FCSTD DOCUMENT  (FreeCAD 0.20R29410 (Git))
Label: plan
License: All rights reserved
LicenseURL: http://en.wikipedia.org/wiki/All_rights_reserved
objects: Sketcher::SketchObject×1, PartDesign::Body×1, Spreadsheet::Sheet×1
note: 2 computed .brp shape members not serialized (recipe doc carries the construction recipe); baked Part::Feature solids carry a one-line shape summary decoded from their .brp

FEATURE [Sketcher::SketchObject] Sketch
  FullyConstrained = true
  MapMode = 5
  Placement = pos=(0,0,0) rot=(1,0,0;1.5708rad)
  Support = -> [XZ_Plane]
  expr: Constraints[105] = <<plan>>#<<data>>.plug_height_adat
  expr: Constraints[114] = <<plan>>#<<data>>.output_h
  expr: Constraints[115] = <<plan>>#<<data>>.output_d
  expr: Constraints[116] = <<plan>>#<<data>>.base_t
  expr: Constraints[157] = <<plan>>#<<data>>.wall_t * 2
  expr: Constraints[173] = <<plan>>#<<data>>.top_row_d
  expr: Constraints[175] = <<plan>>#<<data>>.bot_row_d
  expr: Constraints[176] = <<plan>>#<<data>>.middle_space_d
  expr: Constraints[177] = <<plan>>#<<data>>.topbot_latch_d
  expr: Constraints[183] = <<plan>>#<<data>>.wall_t
  expr: Constraints[189] = <<plan>>#<<data>>.plug_height_audio + <<plan>>#<<data>>.wall_t
  expr: Constraints[190] = <<plan>>#<<data>>.plug_height_usb + <<plan>>#<<data>>.wall_t
  expr: Constraints[6] = <<plan>>#<<data>>.central_d
  expr: Constraints[78] = <<plan>>#<<data>>.plug_height_audio
  expr: Constraints[79] = <<plan>>#<<data>>.es3_h
  expr: Constraints[7] = <<plan>>#<<data>>.central_h
  expr: Constraints[80] = <<plan>>#<<data>>.es6_h
  expr: Constraints[81] = <<plan>>#<<data>>.es7_h
  expr: Constraints[82] = <<plan>>#<<data>>.es3_d
  expr: Constraints[83] = <<plan>>#<<data>>.es6_d
  expr: Constraints[84] = <<plan>>#<<data>>.es7_d
  expr: Constraints[85] = <<plan>>#<<data>>.wall_t
  expr: Constraints[86] = <<plan>>#<<data>>.base_t
  expr: Constraints[87] = <<plan>>#<<data>>.base_t
  expr: Constraints[8] = <<plan>>#<<data>>.case_d
  expr: Constraints[94] = <<plan>>#<<data>>.mungo_d
  expr: Constraints[95] = <<plan>>#<<data>>.mungo_h
  expr: Constraints[96] = <<plan>>#<<data>>.rme_d
  expr: Constraints[97] = <<plan>>#<<data>>.rme_h
  sketch-geometry (67):
    g0: LineSegment StartX=-3.67e-14 StartY=123.2 StartZ=0 EndX=277 EndY=123.2 EndZ=0
    g1: LineSegment StartX=273 StartY=58.2 StartZ=0 EndX=273 EndY=53.2 EndZ=0
    g2: LineSegment StartX=4 StartY=53.2 StartZ=0 EndX=4 EndY=58.2 EndZ=0
    g3: LineSegment StartX=24 StartY=32.88 StartZ=0 EndX=79 EndY=32.88 EndZ=0
    g4: LineSegment StartX=79 StartY=32.88 StartZ=0 EndX=79 EndY=10.88 EndZ=0
    g5: LineSegment StartX=79 StartY=10.88 StartZ=0 EndX=24 EndY=10.88 EndZ=0
    g6: LineSegment StartX=24 StartY=10.88 StartZ=0 EndX=24 EndY=32.88 EndZ=0
    g7: LineSegment StartX=139 StartY=78.2 StartZ=0 EndX=214 EndY=78.2 EndZ=0
    g8: LineSegment StartX=214 StartY=78.2 StartZ=0 EndX=214 EndY=58.2 EndZ=0
    g9: LineSegment StartX=214 StartY=58.2 StartZ=0 EndX=139 EndY=58.2 EndZ=0
    g10: LineSegment StartX=139 StartY=58.2 StartZ=0 EndX=139 EndY=78.2 EndZ=0
    g11: LineSegment StartX=8 StartY=57.88 StartZ=0 EndX=83 EndY=57.88 EndZ=0
    g12: LineSegment StartX=83 StartY=57.88 StartZ=0 EndX=83 EndY=37.88 EndZ=0
    g13: LineSegment StartX=83 StartY=37.88 StartZ=0 EndX=8 EndY=37.88 EndZ=0
    g14: LineSegment StartX=8 StartY=37.88 StartZ=0 EndX=8 EndY=57.88 EndZ=0
    g15: LineSegment StartX=139 StartY=43.04 StartZ=0 EndX=196 EndY=43.04 EndZ=0
    g16: LineSegment StartX=196 StartY=43.04 StartZ=0 EndX=196 EndY=2.4 EndZ=0
    g17: LineSegment StartX=196 StartY=2.4 StartZ=0 EndX=139 EndY=2.4 EndZ=0
    g18: LineSegment StartX=139 StartY=2.4 StartZ=0 EndX=139 EndY=43.04 EndZ=0
    g19: LineSegment StartX=196 StartY=53.2 StartZ=0 EndX=253 EndY=53.2 EndZ=0
    g20: LineSegment StartX=253 StartY=53.2 StartZ=0 EndX=253 EndY=22.72 EndZ=0
    g21: LineSegment StartX=253 StartY=22.72 StartZ=0 EndX=196 EndY=22.72 EndZ=0
    g22: LineSegment StartX=196 StartY=22.72 StartZ=0 EndX=196 EndY=53.2 EndZ=0
    g23: LineSegment StartX=139 StartY=2.4 StartZ=0 EndX=119 EndY=2.4 EndZ=0
    g24: LineSegment StartX=119 StartY=2.4 StartZ=0 EndX=119 EndY=43.04 EndZ=0
    g25: LineSegment StartX=119 StartY=43.04 StartZ=0 EndX=139 EndY=43.04 EndZ=0
    g26: LineSegment StartX=253 StartY=53.2 StartZ=0 EndX=273 EndY=53.2 EndZ=0
    g27: LineSegment StartX=273 StartY=53.2 StartZ=0 EndX=273 EndY=22.72 EndZ=0
    g28: LineSegment StartX=273 StartY=22.72 StartZ=0 EndX=253 EndY=22.72 EndZ=0
    g29: LineSegment StartX=196 StartY=22.72 StartZ=0 EndX=253 EndY=22.72 EndZ=0
    g30: LineSegment StartX=253 StartY=22.72 StartZ=0 EndX=253 EndY=2.4 EndZ=0
    g31: LineSegment StartX=253 StartY=2.4 StartZ=0 EndX=196 EndY=2.4 EndZ=0
    g32: LineSegment StartX=196 StartY=2.4 StartZ=0 EndX=196 EndY=22.72 EndZ=0
    g33: LineSegment StartX=253 StartY=2.4 StartZ=0 EndX=273 EndY=2.4 EndZ=0
    g34: LineSegment StartX=273 StartY=2.4 StartZ=0 EndX=273 EndY=22.72 EndZ=0
    g35: LineSegment StartX=273 StartY=22.72 StartZ=0 EndX=253 EndY=22.72 EndZ=0
    g36: LineSegment StartX=79 StartY=32.88 StartZ=0 EndX=119 EndY=32.88 EndZ=0
    g37: LineSegment StartX=119 StartY=32.88 StartZ=0 EndX=119 EndY=10.88 EndZ=0
    g38: LineSegment StartX=119 StartY=10.88 StartZ=0 EndX=79 EndY=10.88 EndZ=0
    g39: LineSegment StartX=24 StartY=32.88 StartZ=0 EndX=81 EndY=32.88 EndZ=0
    g40: LineSegment StartX=81 StartY=32.88 StartZ=0 EndX=81 EndY=2.4 EndZ=0
    g41: LineSegment StartX=81 StartY=2.4 StartZ=0 EndX=24 EndY=2.4 EndZ=0
    g42: LineSegment StartX=24 StartY=2.4 StartZ=0 EndX=24 EndY=32.88 EndZ=0
    g43: LineSegment StartX=24 StartY=32.88 StartZ=0 EndX=24 EndY=32.88 EndZ=0
    g44: LineSegment StartX=24 StartY=32.88 StartZ=0 EndX=24 EndY=10.88 EndZ=0
    g45: LineSegment StartX=24 StartY=10.88 StartZ=0 EndX=24 EndY=10.88 EndZ=0
    g46: LineSegment StartX=119 StartY=53.2 StartZ=0 EndX=119 EndY=2.4 EndZ=0
    g47: LineSegment StartX=119 StartY=2.4 StartZ=0 EndX=114 EndY=2.4 EndZ=0
    g48: LineSegment StartX=114 StartY=53.2 StartZ=0 EndX=114 EndY=58.2 EndZ=0
    g49: LineSegment StartX=273 StartY=53.2 StartZ=0 EndX=119 EndY=53.2 EndZ=0
    g50: LineSegment StartX=119 StartY=53.2 StartZ=0 EndX=4 EndY=53.2 EndZ=0
    g51: LineSegment StartX=4 StartY=58.2 StartZ=0 EndX=114 EndY=58.2 EndZ=0
    g52: LineSegment StartX=114 StartY=58.2 StartZ=0 EndX=273 EndY=58.2 EndZ=0
    g53: LineSegment StartX=114 StartY=32.88 StartZ=0 EndX=4 EndY=32.88 EndZ=0
    g54: LineSegment StartX=4 StartY=32.88 StartZ=0 EndX=4 EndY=37.88 EndZ=0
    g55: LineSegment StartX=4 StartY=37.88 StartZ=0 EndX=114 EndY=37.88 EndZ=0
    g56: LineSegment StartX=114 StartY=37.88 StartZ=0 EndX=114 EndY=53.2 EndZ=0
    g57: LineSegment StartX=114 StartY=2.4 StartZ=0 EndX=114 EndY=32.88 EndZ=0
    g58: LineSegment StartX=114 StartY=32.88 StartZ=0 EndX=114 EndY=37.88 EndZ=0
    g59: LineSegment StartX=8 StartY=123.2 StartZ=0 EndX=8 EndY=58.2 EndZ=0
    g60: LineSegment StartX=8 StartY=58.2 StartZ=0 EndX=136.5 EndY=58.2 EndZ=0
    g61: LineSegment StartX=136.5 StartY=58.2 StartZ=0 EndX=136.5 EndY=123.2 EndZ=0
    g62: LineSegment StartX=140.5 StartY=123.2 StartZ=0 EndX=140.5 EndY=78.2 EndZ=0
    g63: LineSegment StartX=140.5 StartY=78.2 StartZ=0 EndX=269 EndY=78.2 EndZ=0
    g64: LineSegment StartX=269 StartY=78.2 StartZ=0 EndX=269 EndY=123.2 EndZ=0
    g65: LineSegment StartX=0 StartY=0 StartZ=0 EndX=277 EndY=0 EndZ=0
    g66: LineSegment StartX=277 StartY=0 StartZ=0 EndX=277 EndY=123.2 EndZ=0
  constraints (191):
    c: Coincident(g52,g1)
    c: Coincident(g1,g49)
    c: Coincident(g50,g2)
    c: Coincident(g2,g51)
    c: Vertical(g1)
    c: Vertical(g2)
    c: DistanceX(g51,g52) = 269
    c: DistanceY(g2,g2) = 5
    c: Distance(g0) = 277
    c: Coincident(g3,g4)
    c: Coincident(g4,g5)
    c: Coincident(g5,g6)
    c: Coincident(g6,g3)
    c: Horizontal(g3)
    c: Horizontal(g5)
    c: Vertical(g4)
    c: Vertical(g6)
    c: Coincident(g7,g8)
    c: Coincident(g8,g9)
    c: Coincident(g9,g10)
    c: Coincident(g10,g7)
    c: Horizontal(g7)
    c: Horizontal(g9)
    c: Vertical(g8)
    c: Vertical(g10)
    c: Coincident(g11,g12)
    c: Coincident(g12,g13)
    c: Coincident(g13,g14)
    c: Coincident(g14,g11)
    c: Horizontal(g11)
    c: Horizontal(g13)
    c: Vertical(g12)
    c: Vertical(g14)
    c: Coincident(g15,g16)
    c: Coincident(g16,g17)
    c: Coincident(g17,g18)
    c: Coincident(g18,g15)
    c: Horizontal(g15)
    c: Horizontal(g17)
    c: Vertical(g16)
    c: Coincident(g19,g20)
    c: Coincident(g20,g21)
    c: Coincident(g21,g22)
    c: Coincident(g22,g19)
    c: Horizontal(g19)
    c: Horizontal(g21)
    c: Vertical(g20)
    c: Vertical(g22)
    c: Coincident(g17,g23)
    c: Horizontal(g23)
    c: Coincident(g23,g24)
    c: Vertical(g24)
    c: Coincident(g24,g25)
    c: Coincident(g25,g15)
    c: Horizontal(g25)
    c: Coincident(g19,g26)
    c: Horizontal(g26)
    c: Coincident(g26,g27)
    c: Vertical(g27)
    c: Coincident(g27,g28)
    c: Horizontal(g28)
    c: Coincident(g29,g30)
    c: Coincident(g30,g31)
    c: Coincident(g31,g32)
    c: Coincident(g32,g29)
    c: Horizontal(g29)
    c: Horizontal(g31)
    c: Vertical(g30)
    c: Vertical(g32)
    c: Coincident(g30,g33)
    c: Horizontal(g33)
    c: Coincident(g33,g34)
    c: Vertical(g34)
    c: Coincident(g34,g35)
    c: Coincident(g35,g29)
    c: Horizontal(g35)
    c: Equal(g25,g26)
    c: Equal(g26,g35)
    c: Distance(g25) = 20
    c: Distance(g18) = 40.64
    c: Distance(g20) = 30.48
    c: Distance(g30) = 20.32
    c: Distance(g15) = 57
    c: Distance(g19) = 57
    c: Distance(g29) = 57
    c: DistanceX(g-2,g50) = 4
    c: DistanceY(g17) = 2.4
    c: DistanceY(g-1,g30) = 2.4
    c: Coincident(g28,g20)
    c: Coincident(g29,g20)
    c: PointOnObject(g31,g16)
    c: PointOnObject(g26,g1)
    c: Equal(g7,g11)
    c: Equal(g8,g14)
    c: Distance(g11) = 75
    c: Distance(g14) = 20
    c: Distance(g3) = 55
    c: Distance(g6) = 22
    c: Coincident(g3,g36)
    c: Horizontal(g36)
    c: Coincident(g36,g37)
    c: Vertical(g37)
    c: Coincident(g37,g38)
    c: Coincident(g38,g4)
    c: Horizontal(g38)
    c: Distance(g36) = 40
    c: Coincident(g39,g40)
    c: Coincident(g40,g41)
    c: Coincident(g41,g42)
    c: Coincident(g42,g39)
    c: Horizontal(g39)
    c: Horizontal(g41)
    c: Vertical(g40)
    c: Vertical(g42)
    c: Distance(g42) = 30.48
    c: Distance(g39) = 57
    c: DistanceY(g-1,g41) = 2.4
    c: Coincident(g3,g43)
    c: Horizontal(g43)
    c: Coincident(g43,g44)
    c: Vertical(g44)
    c: Coincident(g44,g45)
    c: Coincident(g45,g5)
    c: Horizontal(g45)
    c: Coincident(g43,g39)
    c: Coincident(g46,g23)
    c: Vertical(g46)
    c: Coincident(g46,g47)
    c: Horizontal(g47)
    c: Coincident(g47,g57)
    c: Coincident(g56,g48)
    c: Vertical(g48)
    c: Coincident(g49,g50)
    c: Horizontal(g49)
    c: Horizontal(g50)
    c: PointOnObject(g19,g49)
    c: PointOnObject(g56,g50)
    c: Coincident(g49,g46)
    c: Coincident(g51,g52)
    c: Horizontal(g51)
    c: Horizontal(g52)
    c: Coincident(g51,g48)
    c: Horizontal(g53)
    c: Coincident(g53,g54)
    c: Coincident(g54,g55)
    c: Horizontal(g55)
    c: Equal(g54,g1)
    c: Equal(g47,g1)
    c: Coincident(g58,g56)
    c: Vertical(g56)
    c: Coincident(g57,g58)
    c: Vertical(g57)
    c: Vertical(g58)
    c: Coincident(g56,g55)
    c: Coincident(g53,g57)
    c: PointOnObject(g53,g36)
    c: Tangent(g2,g54)
    c: DistanceX(g-2,g13) = 8
    c: PointOnObject(g59,g0)
    c: Coincident(g59,g60)
    c: Coincident(g60,g61)
    c: PointOnObject(g61,g0)
    c: PointOnObject(g62,g0)
    c: Coincident(g62,g63)
    c: Coincident(g63,g64)
    c: PointOnObject(g64,g0)
    c: Equal(g64,g62)
    c: Perpendicular(g0,g62)
    c: Parallel(g64,g62)
    c: Parallel(g62,g61)
    c: Parallel(g61,g59)
    c: Equal(g60,g63)
    c: Distance(g63) = 128.5
    c: Distance(g61) = 65
    c: Equal(g61,g59)
    c: Distance(g62) = 45
    c: Distance(g61,g62) = 4
    c: Distance(g0,g64) = 8
    c: Coincident(g-1,g65)
    c: PointOnObject(g65,g-1)
    c: Coincident(g65,g66)
    c: Vertical(g66)
    c: Coincident(g0,g66)
    c: Distance(g1,g66) = 4
    c: PointOnObject(g9,g52)
    c: PointOnObject(g7,g63)
    c: Tangent(g18,g10)
    c: Horizontal(g0)
    c: PointOnObject(g12,g55)
    c: DistanceX(g-2,g39) = 24
    c: DistanceX(g-2,g5) = 24
FEATURE [PartDesign::Body] Body
  Group = -> [Sketch]
  Origin = -> Origin
FEATURE [Spreadsheet::Sheet] Spreadsheet  label="data"
  cells = B1=width; C1=depth; D1=height; E1=hole radius; A2=case (top plane); B2(case_w)=555; C2(case_d)==128.5 * 2 + 2 * topbot_latch_d + middle_space_d; F2=wall thickness; G2(wall_t)=4; A3=top row; C3(top_row_d)=65; F3=top/bottom latch; G3(topbot_latch_d)=8; A4=bottom row; C4(bot_row_d)=45; F4=middle spacer; G4(middle_space_d)=4; A5=central support; B5(central_w)==base_w - 2 * wall_t; C5(central_d)==case_d - 2 * wall_t; D5(central_h)=5; A6=case (bottom plane); B6(base_w)=555; C6(base_d)=289; F6=base thickness; G6(base_t)=2.4; A7=es-6; B7(es6_w)=128.5; C7(es6_d)=57; D7(es6_h)==5.08 * 6; F7=audio plug height; G7(plug_height_audio)=20; A8=es-3; B8(es3_w)=128.5; C8(es3_d)=57; D8(es3_h)==5.08 * 8; A9=es-7; B9(es7_w)=128.5; C9(es7_d)=57; D9(es7_h)==5.08 * 4; F9=adat plug height; G9(plug_height_adat)=40; A10=rme; B10(rme_w)=128; C10(rme_d)=55; D10(rme_h)=22; F10=usb plug height; G10(plug_height_usb)=20; A11=mungo; B11(mungo_w)=450; C11(mungo_d)=75; D11(mungo_h)=20; A12=power socket; A13=speaker; A14=output modules; B14(output_w)=128.5; C14(output_d)=57; D14(output_h)==5.08 * 6
